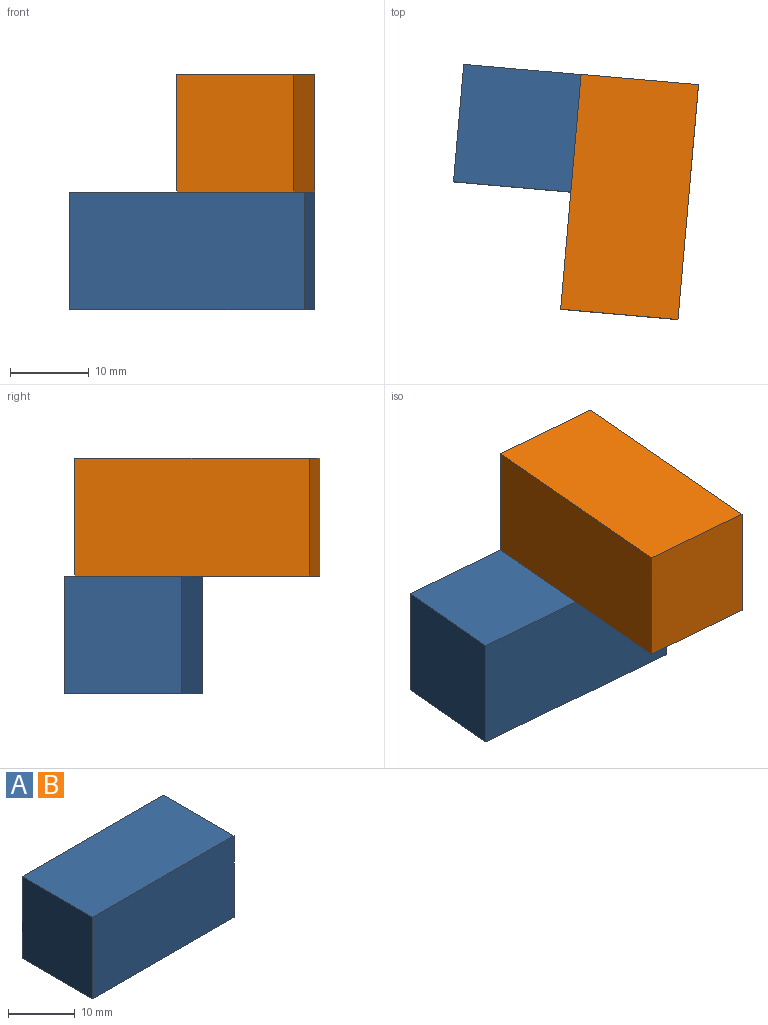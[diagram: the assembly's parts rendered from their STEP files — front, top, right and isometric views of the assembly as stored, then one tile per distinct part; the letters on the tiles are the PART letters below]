
ASSEMBLY  parts=2 mates=1
PART A: 6 faces, bbox 30x15x15 mm
  f0: plane 15x15mm, normal (-1,0,0), area 225mm2, adj f1,f3,f4,f5
  f1: plane 30x15mm, normal (0,0,-1), area 450mm2, adj f0,f2,f4,f5
  f2: plane 15x15mm, normal (1,0,0), area 225mm2, adj f1,f3,f4,f5
  f3: plane 30x15mm, normal (0,0,1), area 450mm2, adj f0,f2,f4,f5
  f4: plane 30x15mm, normal (0,-1,0), area 450mm2, adj f0,f1,f2,f3
  f5: plane 30x15mm, normal (0,1,0), area 450mm2, adj f0,f1,f2,f3
PART B: same geometry as A
PLACE A rot(axis=(0,0,-1),5deg) t=(10.97,8.5,12.36)mm
PLACE B rot(axis=(0,0,1),85deg) t=(23.29,-22.7,27.36)mm
MATE fastened A.f3 <-> B.f1  axis (0,0,1) through (40.85,5.88,27.36)mm
